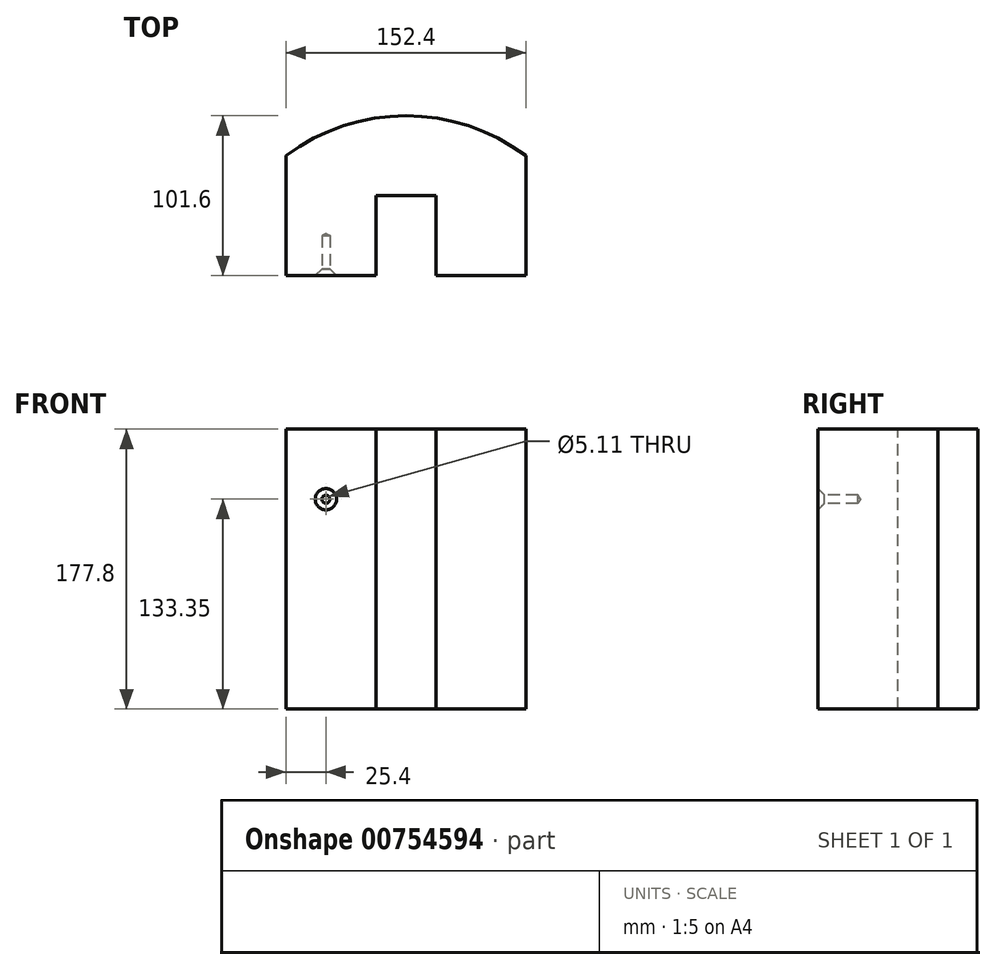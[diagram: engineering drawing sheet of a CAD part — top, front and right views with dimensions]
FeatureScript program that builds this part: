
annotation { "Feature Type Name" : "Feature", "Feature Type Description" : "" }
export const myFeature = defineFeature(function(context is Context, id is Id, definition is map)
    precondition{}
    {
        {
            var Q0;
            Q0=qCreatedBy(makeId("Front.planeOp"),FACE);
            var sketch = newSketch(context, id + "F0", { "sketchPlane" : qUnion([Q0])});
            skLineSegment(sketch, "E0.bottom", {"start": v(-76.2, 88.9) * mm, "end": v(76.2, 88.9) * mm});
            skLineSegment(sketch, "E0.top", {"start": v(-76.2, -88.9) * mm, "end": v(76.2, -88.9) * mm});
            skLineSegment(sketch, "E0.left", {"start": v(-76.2, 88.9) * mm, "end": v(-76.2, -88.9) * mm});
            skLineSegment(sketch, "E0.right", {"start": v(76.2, 88.9) * mm, "end": v(76.2, -88.9) * mm});
            skLineSegment(sketch, "E1", {"start": v(0, 88.9) * mm, "end": v(0, -88.9) * mm, "construction": true});
            skLineSegment(sketch, "E2", {"start": v(-76.2, 0) * mm, "end": v(76.2, 0) * mm, "construction": true});
            skSolve(sketch);
        }
        {
            var Q0;
            Q0=makeQuery(id+"F0.imprint","IMPRINT",FACE,{"disambiguationData":[TD([[makeQuery(id+"F0.imprint","IMPRINT",EDGE,{"derivedFrom":sQuery(id+"F0.wireOp",EDGE,"E0.bottom")}),-1.0]])]});
            extrude(context, id + "F1", {"entities" : qUnion([Q0]), "depth" : 76.2 * mm, "offsetDistance" : 25.4 * mm});
        }
        {
            var Q0;
            Q0=makeQuery(id+"F1.opExtrude","SWEPT_FACE",FACE,{"disambiguationData":[OSD([sQuery(id+"F0.wireOp",EDGE,"E0.bottom")])]});
            var sketch = newSketch(context, id + "F2", { "sketchPlane" : qUnion([Q0])});
            skArc(sketch, "E3", {"start": v(76.2, 0) * mm, "mid": v(0, 25.4) * mm, "end": v(-76.2, 0) * mm});
            skSolve(sketch);
        }
        {
            var Q0;
            Q0=makeQuery(id+"F2.imprint","IMPRINT",FACE,{"disambiguationData":[TD([[makeQuery(id+"F2.imprint","IMPRINT",EDGE,{"derivedFrom":sQuery(id+"F2.wireOp",EDGE,"E3")}),1.0]])]});
            var Q1;
            Q1=makeQuery(id+"F1.opExtrude","SWEPT_FACE",FACE,{"disambiguationData":[OSD([sQuery(id+"F0.wireOp",EDGE,"E0.top")])]});
            var Q2;
            Q2=makeQuery(id+"F1.opExtrude","SWEPT_BODY",BODY,{"disambiguationData":[OSD([sQuery(id+"F0.wireOp",EDGE,"E0.bottom"),sQuery(id+"F0.wireOp",EDGE,"E0.top"),sQuery(id+"F0.wireOp",EDGE,"E0.left"),sQuery(id+"F0.wireOp",EDGE,"E0.right")])]});
            extrude(context, id + "F3", {"entities" : qUnion([Q0]), "operationType" : NewBodyOperationType.ADD, "oppositeDirection" : true, "depth" : 177.8 * mm, "endBoundEntityFace" : qUnion([Q1]), "endBoundEntityBody" : qUnion([Q2]), "offsetDistance" : 25.4 * mm});
        }
        {
            var Q0;
            {var subQ0=sQuery(id+"F0.wireOp",EDGE,"E0.bottom");Q0=makeQuery(id+"F3.boolean.opBoolean","MERGE",FACE,{"derivedFrom":[makeQuery(id+"F1.opExtrude","SWEPT_FACE",FACE,{"disambiguationData":[OSD([subQ0])]}),makeQuery(id+"F3.opExtrude","CAP_FACE",FACE,{"disambiguationData":[OSD([subQ0,sQuery(id+"F2.wireOp",EDGE,"E3")])],"isStart":true})]});}
            var sketch = newSketch(context, id + "F4", { "sketchPlane" : qUnion([Q0])});
            skLineSegment(sketch, "E4", {"start": v(0, 25.4) * mm, "end": v(0, -76.2) * mm, "construction": true});
            skLineSegment(sketch, "E5.right", {"start": v(-19.05, -76.2) * mm, "end": v(-19.05, -25.4) * mm});
            skLineSegment(sketch, "E6", {"start": v(-19.05, -25.4) * mm, "end": v(19.05, -25.4) * mm});
            skLineSegment(sketch, "E7", {"start": v(19.05, -25.4) * mm, "end": v(19.05, -76.2) * mm});
            skLineSegment(sketch, "E8", {"start": v(19.05, -76.2) * mm, "end": v(-19.05, -76.2) * mm});
            skSolve(sketch);
        }
        {
            var Q0;
            Q0=makeQuery(id+"F4.imprint","IMPRINT",FACE,{"disambiguationData":[TD([[makeQuery(id+"F4.imprint","IMPRINT",EDGE,{"derivedFrom":sQuery(id+"F4.wireOp",EDGE,"E5.right")}),-1.0]])]});
            var Q1;
            Q1=makeQuery(id+"F3.boolean.opBoolean","MERGE",FACE,{"derivedFrom":[makeQuery(id+"F1.opExtrude","SWEPT_FACE",FACE,{"disambiguationData":[OSD([sQuery(id+"F0.wireOp",EDGE,"E0.top")])]}),makeQuery(id+"F3.opExtrude","CAP_FACE",FACE,{"disambiguationData":[OSD([sQuery(id+"F0.wireOp",EDGE,"E0.bottom"),sQuery(id+"F2.wireOp",EDGE,"E3")])],"isStart":false})]});
            extrude(context, id + "F5", {"entities" : qUnion([Q0]), "operationType" : NewBodyOperationType.REMOVE, "endBound" : BoundingType.UP_TO_SURFACE, "oppositeDirection" : true, "depth" : 25.4 * mm, "endBoundEntityFace" : qUnion([Q1]), "offsetDistance" : 25.4 * mm});
        }
        {
            var Q0;
            {var subQ1=sQuery(id+"F0.wireOp",EDGE,"E0.bottom");var subQ2=sQuery(id+"F0.wireOp",EDGE,"E0.left");var subQ3=sQuery(id+"F0.wireOp",EDGE,"E0.top");Q0=makeQuery(id+"F5.boolean.opBoolean","SPLIT",FACE,{"disambiguationData":[TD([makeQuery(id+"F1.opExtrude","SWEPT_FACE",FACE,{"disambiguationData":[OSD([subQ2])]})])],"derivedFrom":makeQuery(id+"F1.opExtrude","CAP_FACE",FACE,{"disambiguationData":[OSD([subQ1,subQ3,subQ2,sQuery(id+"F0.wireOp",EDGE,"E0.right")])],"isStart":false})});}
            var sketch = newSketch(context, id + "F6", { "sketchPlane" : qUnion([Q0])});
            skLineSegment(sketch, "E9", {"start": v(0, 88.9) * mm, "end": v(0, -88.9) * mm, "construction": true});
            skLineSegment(sketch, "E10", {"start": v(-76.2, 0) * mm, "end": v(76.2, 0) * mm, "construction": true});
            skPoint(sketch, "E11", {"position": v(-50.8, 44.45) * mm});
            skSolve(sketch);
        }
        {
            var Q0;
            Q0=sQuery(id+"F6.wireOp",VERTEX,"E11");
            var Q1;
            Q1=makeQuery(id+"F1.opExtrude","SWEPT_BODY",BODY,{"disambiguationData":[OSD([sQuery(id+"F0.wireOp",EDGE,"E0.bottom"),sQuery(id+"F0.wireOp",EDGE,"E0.top"),sQuery(id+"F0.wireOp",EDGE,"E0.left"),sQuery(id+"F0.wireOp",EDGE,"E0.right")])]});
            hole(context, id + "F7", {"style" : HoleStyle.C_SINK, "endStyle" : HoleEndStyle.BLIND, "holeDiameter" : 5.1 * mm, "cSinkDiameter" : 13.5 * mm, "cSinkAngle" : 90 * degree, "majorDiameter" : 6.35 * mm, "holeDepth" : 25.4 * mm, "isTappedThrough" : true, "tappedDepth" : 12.7 * mm, "tapClearance" : 3, "startFromSketch" : true, "locations" : qUnion([Q0]), "scope" : qUnion([Q1])});
        }
    });
